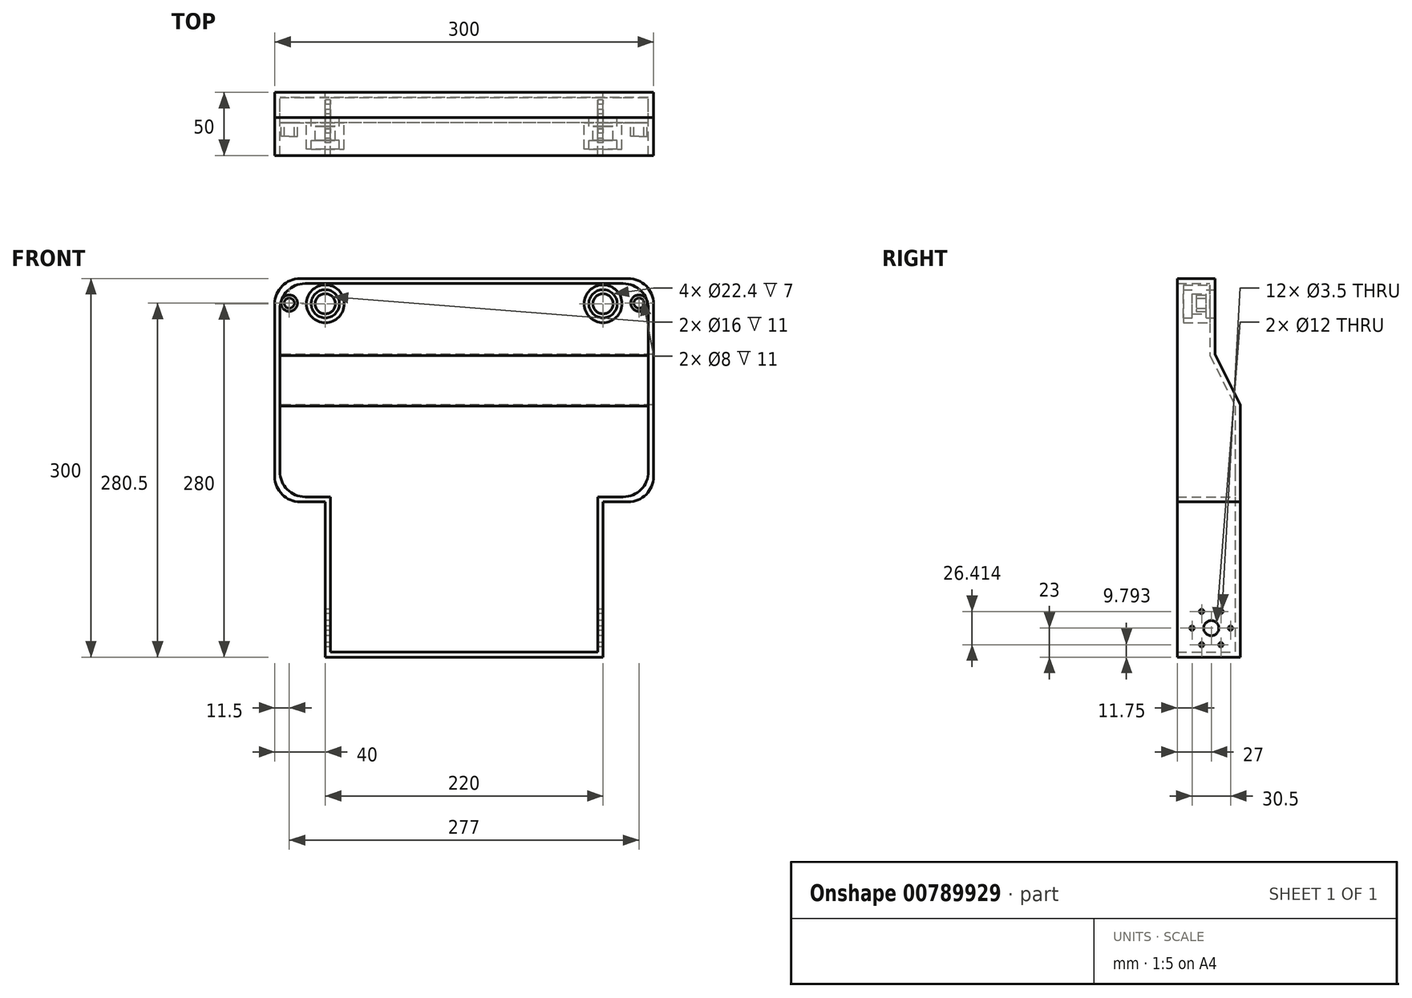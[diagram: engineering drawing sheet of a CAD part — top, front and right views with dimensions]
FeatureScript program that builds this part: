
annotation { "Feature Type Name" : "Feature", "Feature Type Description" : "" }
export const myFeature = defineFeature(function(context is Context, id is Id, definition is map)
    precondition{}
    {
        {
            var Q0;
            Q0=qCreatedBy(makeId("Front.planeOp"),FACE);
            var sketch = newSketch(context, id + "F0", { "sketchPlane" : qUnion([Q0])});
            skLineSegment(sketch, "E0", {"start": v(0, 0) * mm, "end": v(0, -177) * mm});
            skLineSegment(sketch, "E1", {"start": v(0, -177) * mm, "end": v(40, -177) * mm});
            skLineSegment(sketch, "E2", {"start": v(40, -177) * mm, "end": v(40, -300) * mm});
            skLineSegment(sketch, "E3", {"start": v(40, -300) * mm, "end": v(260, -300) * mm});
            skLineSegment(sketch, "E4", {"start": v(260, -300) * mm, "end": v(260, -177) * mm});
            skLineSegment(sketch, "E5", {"start": v(260, -177) * mm, "end": v(300, -177) * mm});
            skLineSegment(sketch, "E6", {"start": v(300, -177) * mm, "end": v(300, 0) * mm});
            skLineSegment(sketch, "E7", {"start": v(300, 0) * mm, "end": v(0, 0) * mm});
            skSolve(sketch);
        }
        {
            var Q0;
            Q0 = qSketchRegion(id + "F0", true);
            extrude(context, id + "F1", {"entities" : qUnion([Q0]), "depth" : 50 * mm, "offsetDistance" : 25 * mm});
        }
        {
            var Q0;
            Q0=qCreatedBy(makeId("Right.planeOp"),FACE);
            var sketch = newSketch(context, id + "F2", { "sketchPlane" : qUnion([Q0])});
            skLineSegment(sketch, "E8", {"start": v(-20, 0) * mm, "end": v(-20, -60) * mm});
            skLineSegment(sketch, "E9", {"start": v(-20, -60) * mm, "end": v(0, -100) * mm});
            skLineSegment(sketch, "E10", {"start": v(0, -100) * mm, "end": v(0, 0) * mm});
            skLineSegment(sketch, "E11", {"start": v(0, 0) * mm, "end": v(-20, 0) * mm});
            skSolve(sketch);
        }
        {
            var Q0;
            Q0=makeQuery(id+"F2.imprint","IMPRINT",FACE,{"disambiguationData":[TD([[makeQuery(id+"F2.imprint","IMPRINT",EDGE,{"derivedFrom":sQuery(id+"F2.wireOp",EDGE,"E8")}),1.0]])]});
            var Q1;
            Q1=sQuery(id+"F2.wireOp",EDGE,"E8");
            var Q2;
            Q2=sQuery(id+"F2.wireOp",EDGE,"E9");
            var Q3;
            Q3=sQuery(id+"F2.wireOp",EDGE,"E10");
            var Q4;
            Q4=sQuery(id+"F2.wireOp",EDGE,"E11");
            extrude(context, id + "F3", {"entities" : qUnion([Q0]), "operationType" : NewBodyOperationType.REMOVE, "surfaceEntities" : qUnion([Q1, Q2, Q3, Q4]), "depth" : 333 * mm, "offsetDistance" : 25 * mm});
        }
        {
            var Q0;
            Q0=makeQuery(id+"F1.opExtrude","CAP_FACE",FACE,{"disambiguationData":[OSD([sQuery(id+"F0.wireOp",EDGE,"E0"),sQuery(id+"F0.wireOp",EDGE,"E1"),sQuery(id+"F0.wireOp",EDGE,"E2"),sQuery(id+"F0.wireOp",EDGE,"E3"),sQuery(id+"F0.wireOp",EDGE,"E4"),sQuery(id+"F0.wireOp",EDGE,"E5"),sQuery(id+"F0.wireOp",EDGE,"E6"),sQuery(id+"F0.wireOp",EDGE,"E7")])],"isStart":false});
            shell(context, id + "F4", {"entities" : qUnion([Q0]), "thickness" : 4 * mm});
        }
        {
            var Q0;
            Q0=qCreatedBy(makeId("Right.planeOp"),FACE);
            var sketch = newSketch(context, id + "F5", { "sketchPlane" : qUnion([Q0])});
            skCircle(sketch, "E12", {"center": v(-23, -277) * mm, "radius": 6 * mm});
            skCircle(sketch, "E13", {"center": v(-23, -277) * mm, "radius": 15.25 * mm});
            skCircle(sketch, "E14", {"center": v(-38.25, -277) * mm, "radius": 1.75 * mm});
            skCircle(sketch, "E15.1.0", {"center": v(-30.62, -290.2) * mm, "radius": 1.75 * mm});
            skCircle(sketch, "E15.2.0", {"center": v(-15.38, -290.2) * mm, "radius": 1.75 * mm});
            skCircle(sketch, "E15.3.0", {"center": v(-7.75, -277) * mm, "radius": 1.75 * mm});
            skCircle(sketch, "E15.4.0", {"center": v(-15.37, -263.8) * mm, "radius": 1.75 * mm});
            skCircle(sketch, "E15.5.0", {"center": v(-30.63, -263.8) * mm, "radius": 1.75 * mm});
            skSolve(sketch);
        }
        {
            var Q0;
            {var subQ0=sQuery(id+"F5.wireOp",EDGE,"E13");var subQ1=sQuery(id+"F5.wireOp",EDGE,"E15.3.0");var subQ2=makeQuery(id+"F5.imprint","INTERSECT",VERTEX,{"disambiguationData":[OD(0.0)],"derivedFrom":[subQ1,subQ0]});Q0=makeQuery(id+"F5.imprint","IMPRINT",FACE,{"disambiguationData":[TD([[makeQuery(id+"F5.imprint","IMPRINT",EDGE,{"disambiguationData":[TD([[subQ2,1.0]])],"derivedFrom":subQ1}),1.0]])]});}
            var Q1;
            {var subQ0=sQuery(id+"F5.wireOp",EDGE,"E13");var subQ1=sQuery(id+"F5.wireOp",EDGE,"E15.4.0");var subQ2=makeQuery(id+"F5.imprint","INTERSECT",VERTEX,{"disambiguationData":[OD(0.0)],"derivedFrom":[subQ1,subQ0]});Q1=makeQuery(id+"F5.imprint","IMPRINT",FACE,{"disambiguationData":[TD([[makeQuery(id+"F5.imprint","IMPRINT",EDGE,{"disambiguationData":[TD([[subQ2,1.0]])],"derivedFrom":subQ1}),1.0]])]});}
            var Q2;
            {var subQ0=sQuery(id+"F5.wireOp",EDGE,"E13");var subQ1=sQuery(id+"F5.wireOp",EDGE,"E15.3.0");var subQ2=makeQuery(id+"F5.imprint","INTERSECT",VERTEX,{"disambiguationData":[OD(0.0)],"derivedFrom":[subQ1,subQ0]});Q2=makeQuery(id+"F5.imprint","IMPRINT",FACE,{"disambiguationData":[TD([[makeQuery(id+"F5.imprint","IMPRINT",EDGE,{"disambiguationData":[TD([[subQ2,-1.0]])],"derivedFrom":subQ1}),1.0]])]});}
            var Q3;
            {var subQ0=sQuery(id+"F5.wireOp",EDGE,"E13");var subQ1=sQuery(id+"F5.wireOp",EDGE,"E15.4.0");var subQ2=makeQuery(id+"F5.imprint","INTERSECT",VERTEX,{"disambiguationData":[OD(0.0)],"derivedFrom":[subQ1,subQ0]});Q3=makeQuery(id+"F5.imprint","IMPRINT",FACE,{"disambiguationData":[TD([[makeQuery(id+"F5.imprint","IMPRINT",EDGE,{"disambiguationData":[TD([[subQ2,-1.0]])],"derivedFrom":subQ1}),1.0]])]});}
            var Q4;
            {var subQ0=sQuery(id+"F5.wireOp",EDGE,"E13");var subQ1=sQuery(id+"F5.wireOp",EDGE,"E15.5.0");var subQ2=makeQuery(id+"F5.imprint","INTERSECT",VERTEX,{"disambiguationData":[OD(0.0)],"derivedFrom":[subQ1,subQ0]});Q4=makeQuery(id+"F5.imprint","IMPRINT",FACE,{"disambiguationData":[TD([[makeQuery(id+"F5.imprint","IMPRINT",EDGE,{"disambiguationData":[TD([[subQ2,-1.0]])],"derivedFrom":subQ1}),1.0]])]});}
            var Q5;
            {var subQ0=sQuery(id+"F5.wireOp",EDGE,"E13");var subQ1=sQuery(id+"F5.wireOp",EDGE,"E15.5.0");var subQ2=makeQuery(id+"F5.imprint","INTERSECT",VERTEX,{"disambiguationData":[OD(0.0)],"derivedFrom":[subQ1,subQ0]});Q5=makeQuery(id+"F5.imprint","IMPRINT",FACE,{"disambiguationData":[TD([[makeQuery(id+"F5.imprint","IMPRINT",EDGE,{"disambiguationData":[TD([[subQ2,1.0]])],"derivedFrom":subQ1}),1.0]])]});}
            var Q6;
            {var subQ0=sQuery(id+"F5.wireOp",EDGE,"E13");var subQ1=sQuery(id+"F5.wireOp",EDGE,"E14");var subQ2=makeQuery(id+"F5.imprint","INTERSECT",VERTEX,{"disambiguationData":[OD(0.0)],"derivedFrom":[subQ1,subQ0]});Q6=makeQuery(id+"F5.imprint","IMPRINT",FACE,{"disambiguationData":[TD([[makeQuery(id+"F5.imprint","IMPRINT",EDGE,{"disambiguationData":[TD([[subQ2,-1.0]])],"derivedFrom":subQ1}),1.0]])]});}
            var Q7;
            {var subQ0=sQuery(id+"F5.wireOp",EDGE,"E13");var subQ1=sQuery(id+"F5.wireOp",EDGE,"E14");var subQ2=makeQuery(id+"F5.imprint","INTERSECT",VERTEX,{"disambiguationData":[OD(0.0)],"derivedFrom":[subQ1,subQ0]});Q7=makeQuery(id+"F5.imprint","IMPRINT",FACE,{"disambiguationData":[TD([[makeQuery(id+"F5.imprint","IMPRINT",EDGE,{"disambiguationData":[TD([[subQ2,1.0]])],"derivedFrom":subQ1}),1.0]])]});}
            var Q8;
            {var subQ0=sQuery(id+"F5.wireOp",EDGE,"E13");var subQ1=sQuery(id+"F5.wireOp",EDGE,"E15.1.0");var subQ2=makeQuery(id+"F5.imprint","INTERSECT",VERTEX,{"disambiguationData":[OD(0.0)],"derivedFrom":[subQ1,subQ0]});Q8=makeQuery(id+"F5.imprint","IMPRINT",FACE,{"disambiguationData":[TD([[makeQuery(id+"F5.imprint","IMPRINT",EDGE,{"disambiguationData":[TD([[subQ2,-1.0]])],"derivedFrom":subQ1}),1.0]])]});}
            var Q9;
            {var subQ0=sQuery(id+"F5.wireOp",EDGE,"E13");var subQ1=sQuery(id+"F5.wireOp",EDGE,"E15.1.0");var subQ2=makeQuery(id+"F5.imprint","INTERSECT",VERTEX,{"disambiguationData":[OD(0.0)],"derivedFrom":[subQ1,subQ0]});Q9=makeQuery(id+"F5.imprint","IMPRINT",FACE,{"disambiguationData":[TD([[makeQuery(id+"F5.imprint","IMPRINT",EDGE,{"disambiguationData":[TD([[subQ2,1.0]])],"derivedFrom":subQ1}),1.0]])]});}
            var Q10;
            {var subQ0=sQuery(id+"F5.wireOp",EDGE,"E13");var subQ1=sQuery(id+"F5.wireOp",EDGE,"E15.2.0");var subQ2=makeQuery(id+"F5.imprint","INTERSECT",VERTEX,{"disambiguationData":[OD(0.0)],"derivedFrom":[subQ1,subQ0]});Q10=makeQuery(id+"F5.imprint","IMPRINT",FACE,{"disambiguationData":[TD([[makeQuery(id+"F5.imprint","IMPRINT",EDGE,{"disambiguationData":[TD([[subQ2,1.0]])],"derivedFrom":subQ1}),1.0]])]});}
            var Q11;
            {var subQ0=sQuery(id+"F5.wireOp",EDGE,"E13");var subQ1=sQuery(id+"F5.wireOp",EDGE,"E15.2.0");var subQ2=makeQuery(id+"F5.imprint","INTERSECT",VERTEX,{"disambiguationData":[OD(0.0)],"derivedFrom":[subQ1,subQ0]});Q11=makeQuery(id+"F5.imprint","IMPRINT",FACE,{"disambiguationData":[TD([[makeQuery(id+"F5.imprint","IMPRINT",EDGE,{"disambiguationData":[TD([[subQ2,-1.0]])],"derivedFrom":subQ1}),1.0]])]});}
            var Q12;
            Q12=makeQuery(id+"F5.imprint","IMPRINT",FACE,{"disambiguationData":[TD([[makeQuery(id+"F5.imprint","IMPRINT",EDGE,{"derivedFrom":sQuery(id+"F5.wireOp",EDGE,"E12")}),1.0]])]});
            var Q13;
            Q13=sQuery(id+"F5.wireOp",EDGE,"E14");
            var Q14;
            Q14=sQuery(id+"F5.wireOp",EDGE,"E15.5.0");
            var Q15;
            Q15=sQuery(id+"F5.wireOp",EDGE,"E15.4.0");
            var Q16;
            Q16=sQuery(id+"F5.wireOp",EDGE,"E15.3.0");
            var Q17;
            Q17=sQuery(id+"F5.wireOp",EDGE,"E15.2.0");
            var Q18;
            Q18=sQuery(id+"F5.wireOp",EDGE,"E15.1.0");
            var Q19;
            Q19=sQuery(id+"F5.wireOp",EDGE,"E12");
            extrude(context, id + "F6", {"entities" : qUnion([Q0, Q1, Q2, Q3, Q4, Q5, Q6, Q7, Q8, Q9, Q10, Q11, Q12]), "operationType" : NewBodyOperationType.REMOVE, "surfaceEntities" : qUnion([Q13, Q14, Q15, Q16, Q17, Q18, Q19]), "depth" : 302.7 * mm, "offsetDistance" : 25 * mm});
        }
        {
            var Q0;
            Q0=makeQuery(id+"F1.opExtrude","SWEPT_EDGE",EDGE,{"disambiguationData":[OSD([sQuery(id+"F0.wireOp",EDGE,"E5"),sQuery(id+"F0.wireOp",EDGE,"E6")])]});
            var Q1;
            Q1=makeQuery(id+"F4.opShell","OFFSET_EDGE",EDGE,{"disambiguationData":[OSD([sQuery(id+"F0.wireOp",EDGE,"E5"),sQuery(id+"F0.wireOp",EDGE,"E6")])]});
            var Q2;
            Q2=makeQuery(id+"F4.opShell","OFFSET_EDGE",EDGE,{"disambiguationData":[OSD([sQuery(id+"F0.wireOp",EDGE,"E0"),sQuery(id+"F0.wireOp",EDGE,"E1")])]});
            var Q3;
            Q3=makeQuery(id+"F1.opExtrude","SWEPT_EDGE",EDGE,{"disambiguationData":[OSD([sQuery(id+"F0.wireOp",EDGE,"E0"),sQuery(id+"F0.wireOp",EDGE,"E1")])]});
            var Q4;
            Q4=makeQuery(id+"F1.opExtrude","SWEPT_EDGE",EDGE,{"disambiguationData":[OSD([sQuery(id+"F0.wireOp",EDGE,"E6"),sQuery(id+"F0.wireOp",EDGE,"E7")])]});
            var Q5;
            Q5=makeQuery(id+"F4.opShell","OFFSET_EDGE",EDGE,{"disambiguationData":[OSD([sQuery(id+"F0.wireOp",EDGE,"E6"),sQuery(id+"F0.wireOp",EDGE,"E7")])]});
            var Q6;
            Q6=makeQuery(id+"F1.opExtrude","SWEPT_EDGE",EDGE,{"disambiguationData":[OSD([sQuery(id+"F0.wireOp",EDGE,"E0"),sQuery(id+"F0.wireOp",EDGE,"E7")])]});
            var Q7;
            Q7=makeQuery(id+"F4.opShell","OFFSET_EDGE",EDGE,{"disambiguationData":[OSD([sQuery(id+"F0.wireOp",EDGE,"E0"),sQuery(id+"F0.wireOp",EDGE,"E7")])]});
            fillet(context, id + "F7", {"entities" : qUnion([Q0, Q1, Q2, Q3, Q4, Q5, Q6, Q7]), "tangentPropagation" : true, "radius" : 20 * mm, "defaultsChanged" : false, "vertexSettings" : [], "allowEdgeOverflow" : false});
        }
        {
            var Q0;
            Q0=qCreatedBy(makeId("Front.planeOp"),FACE);
            var sketch = newSketch(context, id + "F8", { "sketchPlane" : qUnion([Q0])});
            skCircle(sketch, "E16", {"center": v(40, -20) * mm, "radius": 15 * mm});
            skCircle(sketch, "E17", {"center": v(40, -20) * mm, "radius": 11.2 * mm});
            skCircle(sketch, "E18", {"center": v(40, -20) * mm, "radius": 8 * mm});
            skCircle(sketch, "E19", {"center": v(260, -20) * mm, "radius": 15 * mm});
            skCircle(sketch, "E20", {"center": v(260, -20) * mm, "radius": 11.2 * mm});
            skCircle(sketch, "E21", {"center": v(260, -20) * mm, "radius": 8 * mm});
            skSolve(sketch);
        }
        {
            var Q0;
            Q0=makeQuery(id+"F8.imprint","IMPRINT",FACE,{"disambiguationData":[TD([[makeQuery(id+"F8.imprint","IMPRINT",EDGE,{"derivedFrom":sQuery(id+"F8.wireOp",EDGE,"E16")}),1.0]])]});
            var Q1;
            Q1=makeQuery(id+"F8.imprint","IMPRINT",FACE,{"disambiguationData":[TD([[makeQuery(id+"F8.imprint","IMPRINT",EDGE,{"derivedFrom":sQuery(id+"F8.wireOp",EDGE,"E19")}),1.0]])]});
            extrude(context, id + "F9", {"entities" : qUnion([Q0, Q1]), "operationType" : NewBodyOperationType.ADD, "depth" : 45 * mm, "offsetDistance" : 25 * mm, "hasSecondDirection" : true, "secondDirectionOppositeDirection" : false, "secondDirectionDepth" : 20 * mm});
        }
        {
            var Q0;
            Q0=makeQuery(id+"F8.imprint","IMPRINT",FACE,{"disambiguationData":[TD([[makeQuery(id+"F8.imprint","IMPRINT",EDGE,{"derivedFrom":sQuery(id+"F8.wireOp",EDGE,"E17")}),1.0]])]});
            var Q1;
            Q1=makeQuery(id+"F8.imprint","IMPRINT",FACE,{"disambiguationData":[TD([[makeQuery(id+"F8.imprint","IMPRINT",EDGE,{"derivedFrom":sQuery(id+"F8.wireOp",EDGE,"E20")}),1.0]])]});
            extrude(context, id + "F10", {"entities" : qUnion([Q0, Q1]), "operationType" : NewBodyOperationType.ADD, "depth" : 38 * mm, "offsetDistance" : 25 * mm, "hasSecondDirection" : true, "secondDirectionOppositeDirection" : false, "secondDirectionDepth" : 27 * mm});
        }
        {
            var Q0;
            Q0=makeQuery(id+"F8.imprint","IMPRINT",FACE,{"disambiguationData":[TD([[makeQuery(id+"F8.imprint","IMPRINT",EDGE,{"derivedFrom":sQuery(id+"F8.wireOp",EDGE,"E18")}),1.0]])]});
            var Q1;
            Q1=makeQuery(id+"F8.imprint","IMPRINT",FACE,{"disambiguationData":[TD([[makeQuery(id+"F8.imprint","IMPRINT",EDGE,{"derivedFrom":sQuery(id+"F8.wireOp",EDGE,"E21")}),1.0]])]});
            extrude(context, id + "F11", {"entities" : qUnion([Q0, Q1]), "operationType" : NewBodyOperationType.REMOVE, "depth" : 117.9 * mm, "offsetDistance" : 25 * mm});
        }
        {
            var Q0;
            Q0=makeQuery(id+"F8.imprint","IMPRINT",FACE,{"disambiguationData":[TD([[makeQuery(id+"F8.imprint","IMPRINT",EDGE,{"derivedFrom":sQuery(id+"F8.wireOp",EDGE,"E17")}),1.0]])]});
            var Q1;
            Q1=makeQuery(id+"F8.imprint","IMPRINT",FACE,{"disambiguationData":[TD([[makeQuery(id+"F8.imprint","IMPRINT",EDGE,{"derivedFrom":sQuery(id+"F8.wireOp",EDGE,"E20")}),1.0]])]});
            extrude(context, id + "F12", {"entities" : qUnion([Q0, Q1]), "operationType" : NewBodyOperationType.REMOVE, "depth" : 24 * mm, "offsetDistance" : 25 * mm});
        }
        {
            var Q0;
            Q0=qCreatedBy(makeId("Front.planeOp"),FACE);
            var sketch = newSketch(context, id + "F13", { "sketchPlane" : qUnion([Q0])});
            skCircle(sketch, "E22", {"center": v(11.5, -19.5) * mm, "radius": 4 * mm});
            skCircle(sketch, "E23", {"center": v(11.5, -19.5) * mm, "radius": 6.5 * mm});
            skCircle(sketch, "E24", {"center": v(288.5, -19.5) * mm, "radius": 4 * mm});
            skCircle(sketch, "E25", {"center": v(288.5, -19.5) * mm, "radius": 6.5 * mm});
            skSolve(sketch);
        }
        {
            var Q0;
            Q0=makeQuery(id+"F13.imprint","IMPRINT",FACE,{"disambiguationData":[TD([[makeQuery(id+"F13.imprint","IMPRINT",EDGE,{"derivedFrom":sQuery(id+"F13.wireOp",EDGE,"E24")}),-1.0]])]});
            var Q1;
            Q1=makeQuery(id+"F13.imprint","IMPRINT",FACE,{"disambiguationData":[TD([[makeQuery(id+"F13.imprint","IMPRINT",EDGE,{"derivedFrom":sQuery(id+"F13.wireOp",EDGE,"E22")}),-1.0]])]});
            extrude(context, id + "F14", {"entities" : qUnion([Q0, Q1]), "operationType" : NewBodyOperationType.ADD, "depth" : 35 * mm, "offsetDistance" : 25 * mm, "hasSecondDirection" : true, "secondDirectionOppositeDirection" : false, "secondDirectionDepth" : 20 * mm});
        }
    });
